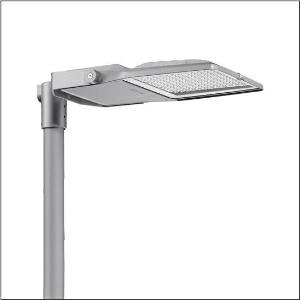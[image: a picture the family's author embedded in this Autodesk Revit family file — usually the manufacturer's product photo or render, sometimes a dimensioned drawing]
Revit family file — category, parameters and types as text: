
# Revit family: floodlight_fl_21_iq_midi___pl52_5xa7782e2d3a_7997
name_source: partatom
category: Lighting Fixtures
units: mm (PartAtom-declared; Revit-internal decimal feet)

## family parameters
Cut with Voids When Loaded = No
Host = Face
Light Source = No
Part Type = Normal
Room Calculation Point = No
Round Connector Dimension = Use Diameter
Shared = No

## types (1)
- --- (1 x LED, 26850 lm, 208.1 W, 3000K)
    Apparent Load = 208 VA
    CIE Flux Codes = 26 60 98 100 100
    Color Rendering = 70
    Color Temperature = 3000K
    Default Elevation = 1800 mm
    Description = Floodlight FL 21 iQ midi, floodlight, primary light control with lens, of PMMA, primary optical cover: protective disc, of toughened safety glass, transparent, light distribution: PL52, light emission: direct distribution, installation type: surface-mounted, lamps: LED, High Power LED, rated values: 26.850lm | 208,1W | 129lm/W (begin service life); end service life: 26.850lm | 227,1W; at 50% lumin. flux: 13.425lm | 90,1W | 149lm/W, colour temperature: 3000K, colour rendering: CRI > 70, light colour: 730, light setting 1 begin service life: 100% | 26.850lm | 208,1W | 129lm/W | 3.000K, light setting 1 end service life: 227,1W, further light settings possible, control: optimised constant luminous flux control (CLO 2.0), Desk-Remote (wireless, voltage-free reading and setting of iQ features in the workshop via application-optimized NFC function/RFID function), Smart-Wire, Night-Set, Temp-Guard, Auto-Match, Street-Remote, pre-setting: linear dimming characteristic, with terminal, 6-pole, mains connection: 220..240V, AC, 50/60Hz, luminaire housing, of diecast aluminium, powder-coated, SITECO metallic grey (DB 702S), corrosivity category C5 mid according to DIN EN ISO 12944suitable for swimming poolschlorine-resistant, sealing non-destructively replaceable, please order mast flange separately, mast bracket, of steel, galvanised, powder-coated, SITECO metallic grey (DB 702S), protection rating (complete): IP66, insulation class (complete): insulation class II (safety insulation), certification: CE, ENEC, VDE, protection symbol: D, impact resistance: IK08, permissible operating ambient temperature: -40..+40°C, permissible operating ambient temperature for outdoor applications: -40..+50°C, standard: DIN EN 12944, LABS conformity tested according to VDMA 24364:2018-05, packaging unit: 1 piece

Light Distribution: PL52
    Height = 76 mm
    Lamp = 1 x LED
    Lamp Light Flux = 26850 lm
    Lamp Power = 208.1 W
    Lamp count = 1
    Length = 657 mm
    Luminous efficacy = 129 lm/W
    Manufacturer = Siteco
    ModVariant = No
    Model = 5XA7782E2D3A
    Mounting Place = Pole
    Mounting Type = Pole annexe
    Number of Poles = 1
    OnlyDefault = Yes
    Power Factor = 1
    Product Name = Floodlight FL 21 iQ midi | PL52
    Product group = floodlight | pylon annexe
    ProductGroupID = 6201
    Protection Class = Protection class II
    Protection Degree = IP 66
    RLX_Detail_Level = 1
    RLX_Emergency_Light_Flux = 0 lm
    RLX_Emergency_Type = 0
    RLX_Emergency_Type_DB = No
    RlxData = <blob elided: 154093 chars, md5=233a3b13>
    Socket = socket
    Standby Power = 0 W
    System Light Flux = 26850 lm
    System Power = 208 W
    Type Comments = factory setting: luminous flux: 100 % | dim-lin: 254 | 710 mA
    Type Image = l_1007123.jpg
    URL = http://relux.com
    VarID = @adj_107587
    Voltage = 0 V
    Weight = 0.00 kg
    Width = 442 mm

## geometry (parser evidence)
native form markers: Blend x4, Sweep x13
no freeform markers — native parametric forms only
